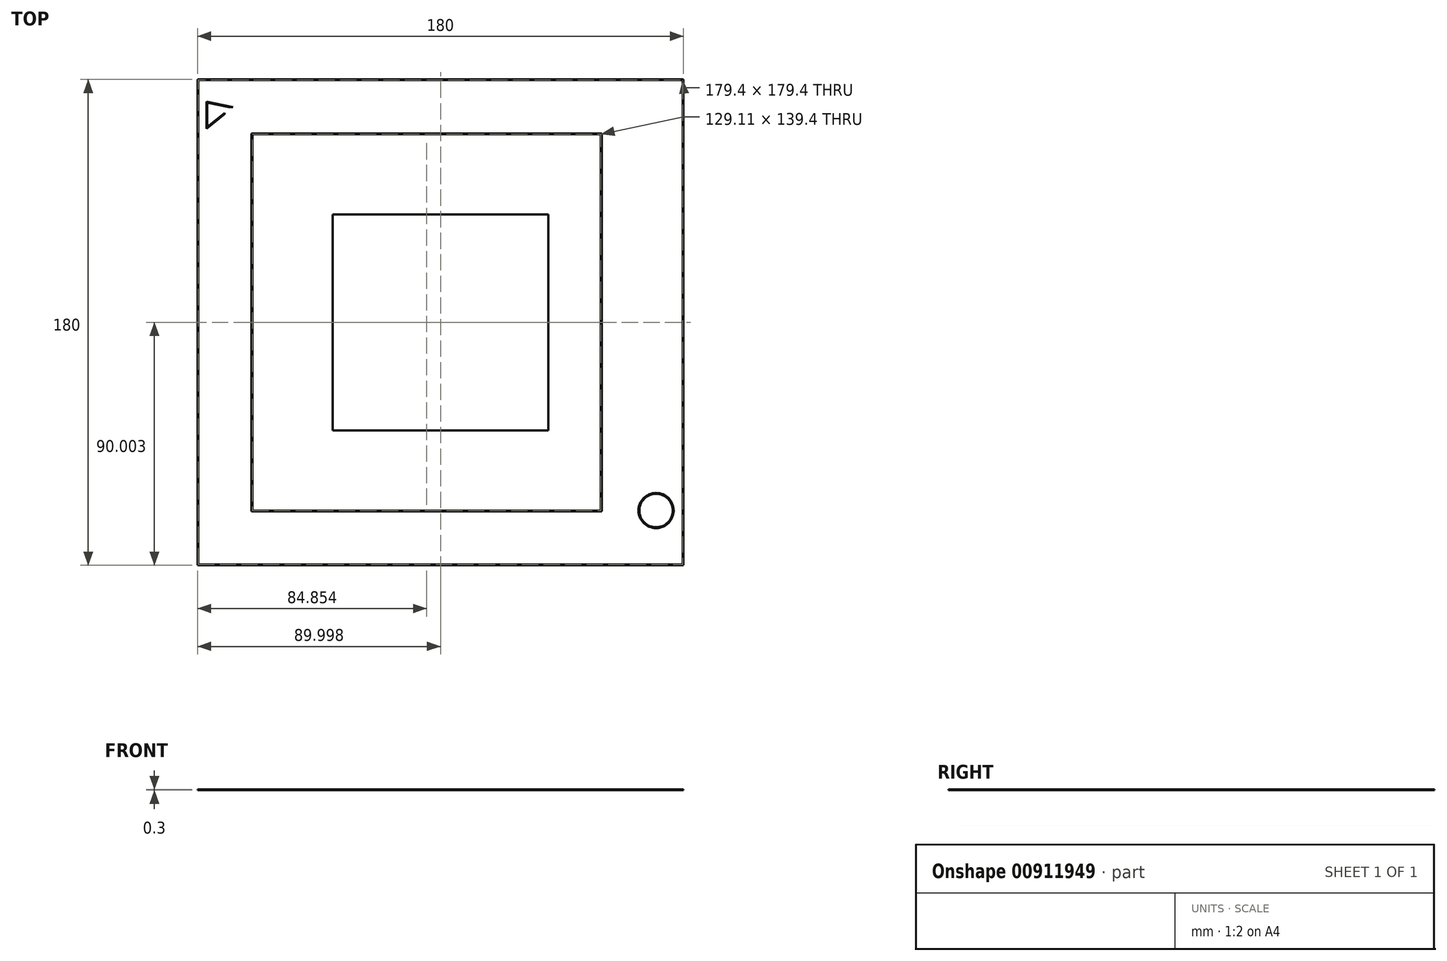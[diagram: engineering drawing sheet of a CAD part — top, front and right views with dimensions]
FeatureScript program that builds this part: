
annotation { "Feature Type Name" : "Feature", "Feature Type Description" : "" }
export const myFeature = defineFeature(function(context is Context, id is Id, definition is map)
    precondition{}
    {
        {
            assignVariable(context, id + "F0", {"name" : "LineHeight", "anyValue" : 0.3});
        }
        {
            var Q0;
            Q0=qCreatedBy(makeId("Top.planeOp"),FACE);
            var sketch = newSketch(context, id + "F1", { "sketchPlane" : qUnion([Q0])});
            skLineSegment(sketch, "E0.bottom", {"start": v(-91.48, 107.86) * mm, "end": v(88.52, 107.86) * mm});
            skLineSegment(sketch, "E0.top", {"start": v(-91.48, -72.14) * mm, "end": v(88.52, -72.14) * mm});
            skLineSegment(sketch, "E0.left", {"start": v(-91.48, 107.86) * mm, "end": v(-91.48, -72.14) * mm});
            skLineSegment(sketch, "E0.right", {"start": v(88.52, 107.86) * mm, "end": v(88.52, -72.14) * mm});
            skLineSegment(sketch, "E1.bottom", {"start": v(-81.48, 97.86) * mm, "end": v(68.23, 97.86) * mm});
            skLineSegment(sketch, "E1.top", {"start": v(-81.48, -62.14) * mm, "end": v(68.23, -62.14) * mm});
            skLineSegment(sketch, "E1.left", {"start": v(-81.48, 97.86) * mm, "end": v(-81.48, -62.14) * mm});
            skLineSegment(sketch, "E1.right", {"start": v(68.23, 97.86) * mm, "end": v(68.23, -62.14) * mm});
            skLineSegment(sketch, "E2.bottom", {"start": v(-71.48, 87.86) * mm, "end": v(58.23, 87.86) * mm});
            skLineSegment(sketch, "E2.top", {"start": v(-71.48, -52.14) * mm, "end": v(58.23, -52.14) * mm});
            skLineSegment(sketch, "E2.left", {"start": v(-71.48, 87.86) * mm, "end": v(-71.48, -52.14) * mm});
            skLineSegment(sketch, "E2.right", {"start": v(58.23, 87.86) * mm, "end": v(58.23, -52.14) * mm});
            skLineSegment(sketch, "E3.bottom", {"start": v(-41.48, 57.86) * mm, "end": v(38.52, 57.86) * mm});
            skLineSegment(sketch, "E3.top", {"start": v(-41.48, -22.14) * mm, "end": v(38.52, -22.14) * mm});
            skLineSegment(sketch, "E3.left", {"start": v(-41.48, 57.86) * mm, "end": v(-41.48, -22.14) * mm});
            skLineSegment(sketch, "E3.right", {"start": v(38.52, 57.86) * mm, "end": v(38.52, -22.14) * mm});
            skLineSegment(sketch, "E4", {"start": v(-88.18, 99.56) * mm, "end": v(-88.18, 89.56) * mm});
            skLineSegment(sketch, "E5", {"start": v(-88.18, 89.56) * mm, "end": v(-78.38, 97.56) * mm});
            skLineSegment(sketch, "E6", {"start": v(-78.38, 97.56) * mm, "end": v(-88.18, 99.56) * mm});
            skCircle(sketch, "E7", {"center": v(78.37, -51.84) * mm, "radius": 6.5 * mm});
            skLineSegment(sketch, "E8", {"start": v(68.23, -51.84) * mm, "end": v(88.52, -51.84) * mm, "construction": true});
            skLineSegment(sketch, "E9", {"start": v(-91.18, 107.56) * mm, "end": v(88.22, 107.56) * mm});
            skLineSegment(sketch, "E10", {"start": v(88.22, 107.56) * mm, "end": v(88.22, -71.84) * mm});
            skLineSegment(sketch, "E11", {"start": v(88.22, -71.84) * mm, "end": v(-91.18, -71.84) * mm});
            skLineSegment(sketch, "E12", {"start": v(-91.18, -71.84) * mm, "end": v(-91.18, 107.56) * mm});
            skLineSegment(sketch, "E13", {"start": v(-81.18, 97.56) * mm, "end": v(67.93, 97.56) * mm});
            skLineSegment(sketch, "E14", {"start": v(67.93, 97.56) * mm, "end": v(67.93, -61.84) * mm});
            skLineSegment(sketch, "E15", {"start": v(67.93, -61.84) * mm, "end": v(-81.18, -61.84) * mm});
            skLineSegment(sketch, "E16", {"start": v(-81.18, -61.84) * mm, "end": v(-81.18, 97.56) * mm});
            skLineSegment(sketch, "E17", {"start": v(-71.18, 87.56) * mm, "end": v(57.93, 87.56) * mm});
            skLineSegment(sketch, "E18", {"start": v(57.93, 87.56) * mm, "end": v(57.93, -51.84) * mm});
            skLineSegment(sketch, "E19", {"start": v(57.93, -51.84) * mm, "end": v(-71.18, -51.84) * mm});
            skLineSegment(sketch, "E20", {"start": v(-71.18, -51.84) * mm, "end": v(-71.18, 87.56) * mm});
            skCircle(sketch, "E21", {"center": v(78.37, -51.84) * mm, "radius": 6.2 * mm});
            skLineSegment(sketch, "E22", {"start": v(-87.88, 99.2) * mm, "end": v(-79.06, 97.4) * mm});
            skPoint(sketch, "E22.startSnap0", {"position": v(-85.81, 99.2) * mm});
            skLineSegment(sketch, "E23", {"start": v(-79.06, 97.4) * mm, "end": v(-87.88, 90.2) * mm});
            skLineSegment(sketch, "E24", {"start": v(-87.88, 90.2) * mm, "end": v(-87.88, 99.2) * mm});
            skSolve(sketch);
        }
        {
            var Q0;
            Q0=makeQuery(id+"F1.imprint","IMPRINT",FACE,{"disambiguationData":[TD([[makeQuery(id+"F1.imprint","IMPRINT",EDGE,{"derivedFrom":sQuery(id+"F1.wireOp",EDGE,"E0.bottom")}),-1.0]])]});
            var Q1;
            Q1=makeQuery(id+"F1.imprint","IMPRINT",FACE,{"disambiguationData":[TD([[makeQuery(id+"F1.imprint","IMPRINT",EDGE,{"derivedFrom":sQuery(id+"F1.wireOp",EDGE,"E1.bottom")}),-1.0]])]});
            var Q2;
            Q2=makeQuery(id+"F1.imprint","IMPRINT",FACE,{"disambiguationData":[TD([[makeQuery(id+"F1.imprint","IMPRINT",EDGE,{"derivedFrom":sQuery(id+"F1.wireOp",EDGE,"E2.bottom")}),-1.0]])]});
            var Q3;
            Q3=makeQuery(id+"F1.imprint","IMPRINT",FACE,{"disambiguationData":[TD([[makeQuery(id+"F1.imprint","IMPRINT",EDGE,{"derivedFrom":sQuery(id+"F1.wireOp",EDGE,"E7")}),1.0]])]});
            var Q4;
            Q4=makeQuery(id+"F1.imprint","IMPRINT",FACE,{"disambiguationData":[TD([[makeQuery(id+"F1.imprint","IMPRINT",EDGE,{"derivedFrom":sQuery(id+"F1.wireOp",EDGE,"E3.bottom")}),-1.0]])]});
            var Q5;
            Q5=makeQuery(id+"F1.imprint","IMPRINT",FACE,{"disambiguationData":[TD([[makeQuery(id+"F1.imprint","IMPRINT",EDGE,{"derivedFrom":sQuery(id+"F1.wireOp",EDGE,"E4")}),1.0]])]});
            extrude(context, id + "F2", {"entities" : qUnion([Q0, Q1, Q2, Q3, Q4, Q5]), "depth" : (getVariable(context, 'LineHeight')) * mm, "offsetDistance" : 25 * mm});
        }
    });
